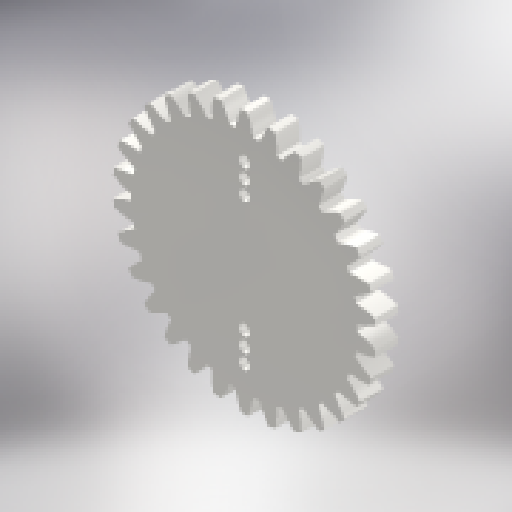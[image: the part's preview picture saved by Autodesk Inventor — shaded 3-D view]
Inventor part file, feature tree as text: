
AUTODESK INVENTOR PART (.ipt)
format: ipt  version: 2024 (Build 280153000, 153)  size: 498,176 bytes
history: native  units: mm (DEFAULTED — no unit token found)
features: extrude x3, plane x3, other x3, sketch x2
ambient origin geometry x8: Origin, YZ Plane, XZ Plane, XY Plane, X Axis, Y Axis, Z Axis, Center Point
bodies: Solid1 (feature_tree)
feature tree (11):
  extrude  "Extrusion1"  Depth=3.175mm TaperAngle=0.0deg
  plane  "Work Plane1"
  plane  "Work Plane2"
  plane  "Work Plane3"
  other  "Spur Gear"
  sketch  "Sketch3"  dims[d3=33.75mm d4=76.2mm d5=0.0mm d6=0.0mm d7=1.047198mm d9=0.0mm d14=0.0mm d15=25.4mm d16=0.0mm d17=0.0mm d18=0.0mm d19=25.4mm d20=3.0mm d21=3.0mm d22=24.0mm d23=5.5mm d24=0.2mm d27=1.5mm d28=1.0mm d29=1.5mm d30=1.5mm d31=1.0mm d32=1.0mm d33=1.0mm d34=1.0mm d35=20.0mm d37=360.0deg d39=1.5mm d40=0.0mm d41=0.0mm d42=0.0mm]
  extrude  "Extrusion2"  Depth=1.5mm TaperAngle=0.0deg
  extrude  "Extrusion3"  Depth=1.5mm TaperAngle=0.0deg
  sketch  "Sketch1"  dims[d0=36.178255mm d1=3.175mm d2=0.0mm]
  other  "Srf1"
  other  "Pitch Diameter"
